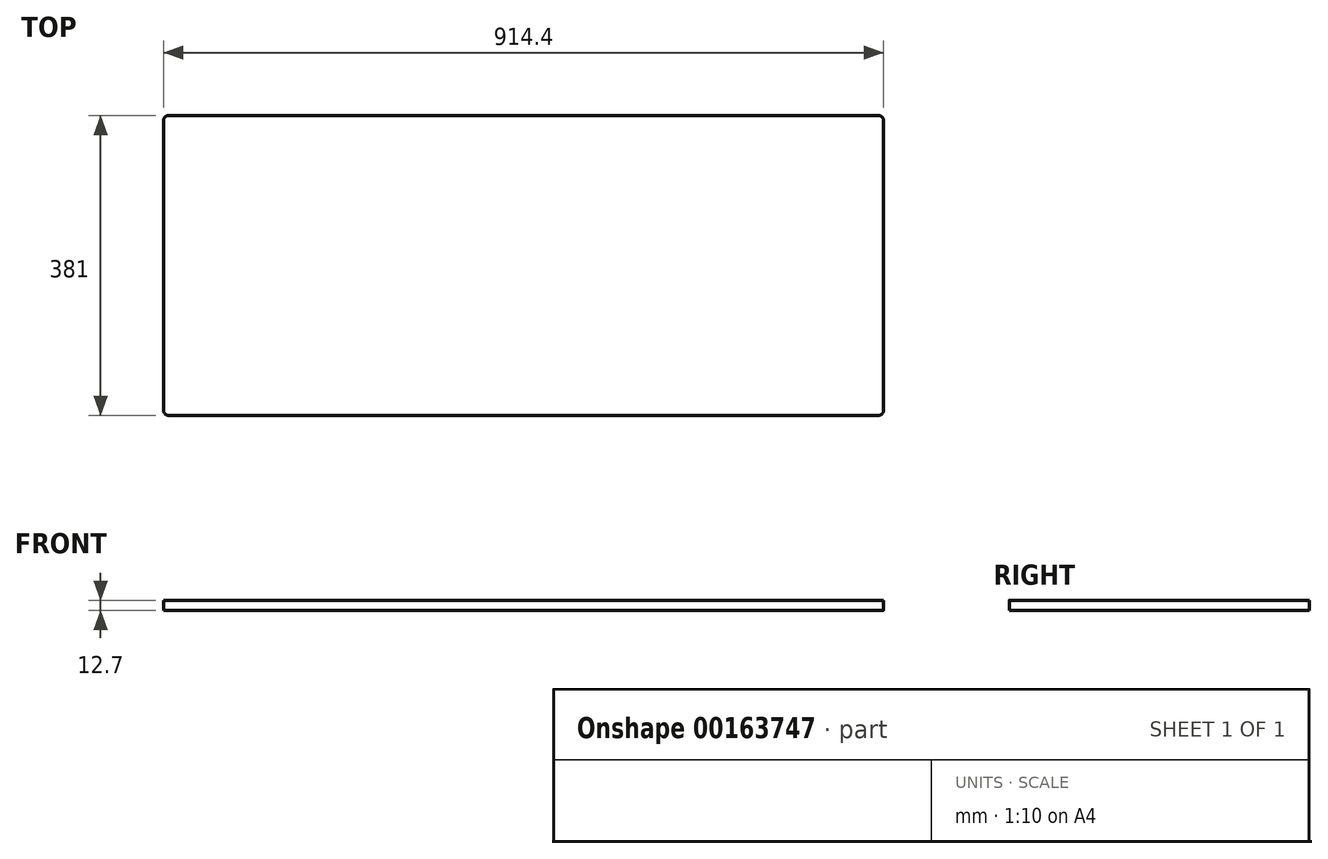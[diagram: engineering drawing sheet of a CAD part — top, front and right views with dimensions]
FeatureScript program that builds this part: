
annotation { "Feature Type Name" : "Feature", "Feature Type Description" : "" }
export const myFeature = defineFeature(function(context is Context, id is Id, definition is map)
    precondition{}
    {
        {
            var Q0;
            Q0=qCreatedBy(makeId("Top.planeOp"),FACE);
            var sketch = newSketch(context, id + "F0", { "sketchPlane" : qUnion([Q0])});
            skLineSegment(sketch, "E0.bottom", {"start": v(-450.85, 190.5) * mm, "end": v(450.85, 190.5) * mm});
            skLineSegment(sketch, "E0.top", {"start": v(-450.85, -190.5) * mm, "end": v(450.85, -190.5) * mm});
            skLineSegment(sketch, "E0.left", {"start": v(-457.2, 184.15) * mm, "end": v(-457.2, -184.15) * mm});
            skLineSegment(sketch, "E0.right", {"start": v(457.2, 184.15) * mm, "end": v(457.2, -184.15) * mm});
            skPoint(sketch, "E0.middle", {"position": v(0, 0) * mm});
            skPoint(sketch, "E1.visualSharp", {"position": v(-457.2, 190.5) * mm});
            skArc(sketch, "E1.filletArc", {"start": v(-450.85, 190.5) * mm, "mid": v(-455.34, 188.64) * mm, "end": v(-457.2, 184.15) * mm});
            skPoint(sketch, "E2.visualSharp", {"position": v(457.2, 190.5) * mm});
            skArc(sketch, "E2.filletArc", {"start": v(457.2, 184.15) * mm, "mid": v(455.34, 188.64) * mm, "end": v(450.85, 190.5) * mm});
            skPoint(sketch, "E3.visualSharp", {"position": v(457.2, -190.5) * mm});
            skArc(sketch, "E3.filletArc", {"start": v(450.85, -190.5) * mm, "mid": v(455.34, -188.64) * mm, "end": v(457.2, -184.15) * mm});
            skPoint(sketch, "E4.visualSharp", {"position": v(-457.2, -190.5) * mm});
            skArc(sketch, "E4.filletArc", {"start": v(-457.2, -184.15) * mm, "mid": v(-455.34, -188.64) * mm, "end": v(-450.85, -190.5) * mm});
            skSolve(sketch);
        }
        {
            var Q0;
            Q0 = qSketchRegion(id + "F0", true);
            extrude(context, id + "F1", {"entities" : qUnion([Q0]), "depth" : 12.7 * mm});
        }
    });
